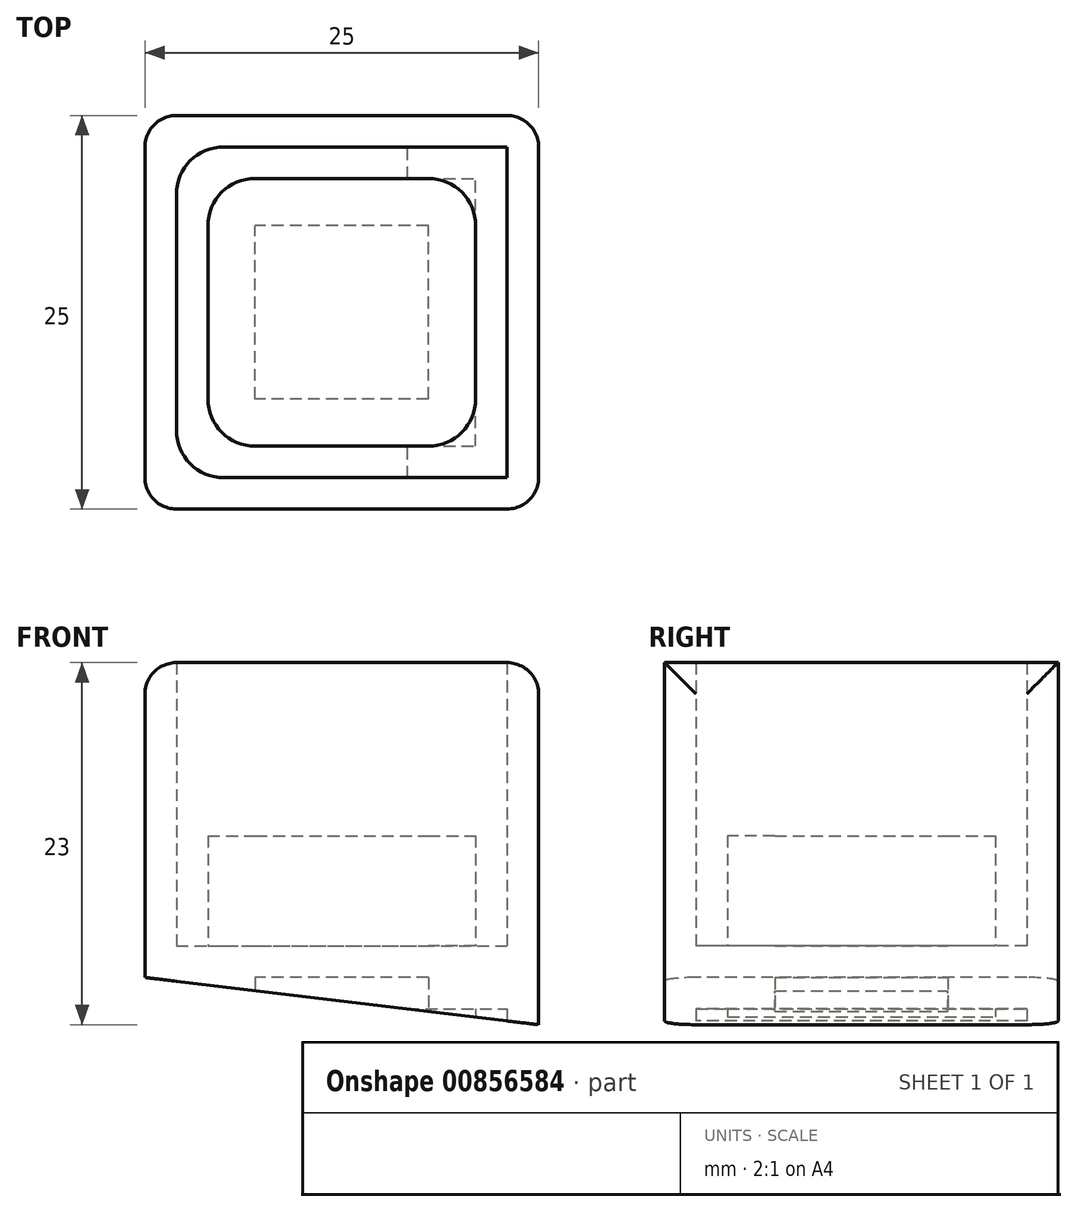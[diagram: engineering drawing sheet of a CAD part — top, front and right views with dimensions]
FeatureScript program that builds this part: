
annotation { "Feature Type Name" : "Feature", "Feature Type Description" : "" }
export const myFeature = defineFeature(function(context is Context, id is Id, definition is map)
    precondition{}
    {
        {
            var Q0;
            Q0=qCreatedBy(makeId("Top.planeOp"),FACE);
            var sketch = newSketch(context, id + "F0", { "sketchPlane" : qUnion([Q0])});
            skLineSegment(sketch, "E0.bottom", {"start": v(0, 0) * mm, "end": v(25, 0) * mm});
            skLineSegment(sketch, "E0.top", {"start": v(0, -25) * mm, "end": v(25, -25) * mm});
            skLineSegment(sketch, "E0.left", {"start": v(0, 0) * mm, "end": v(0, -25) * mm});
            skLineSegment(sketch, "E0.right", {"start": v(25, 0) * mm, "end": v(25, -25) * mm});
            skLineSegment(sketch, "E1.bottom", {"start": v(2, -2) * mm, "end": v(23, -2) * mm});
            skLineSegment(sketch, "E1.top", {"start": v(2, -23) * mm, "end": v(23, -23) * mm});
            skLineSegment(sketch, "E1.left", {"start": v(2, -2) * mm, "end": v(2, -23) * mm});
            skLineSegment(sketch, "E1.right", {"start": v(23, -2) * mm, "end": v(23, -23) * mm});
            skLineSegment(sketch, "E2.bottom", {"start": v(4, -21) * mm, "end": v(21, -21) * mm});
            skLineSegment(sketch, "E2.top", {"start": v(4, -4) * mm, "end": v(21, -4) * mm});
            skLineSegment(sketch, "E2.left", {"start": v(4, -21) * mm, "end": v(4, -4) * mm});
            skLineSegment(sketch, "E2.right", {"start": v(21, -21) * mm, "end": v(21, -4) * mm});
            skLineSegment(sketch, "E3.bottom", {"start": v(18, -18) * mm, "end": v(7, -18) * mm});
            skLineSegment(sketch, "E3.top", {"start": v(18, -7) * mm, "end": v(7, -7) * mm});
            skLineSegment(sketch, "E3.left", {"start": v(18, -18) * mm, "end": v(18, -7) * mm});
            skLineSegment(sketch, "E3.right", {"start": v(7, -18) * mm, "end": v(7, -7) * mm});
            skSolve(sketch);
        }
        {
            var Q0;
            Q0 = qSketchRegion(id + "F0", true);
            extrude(context, id + "F1", {"entities" : qUnion([Q0]), "depth" : 23 * mm, "offsetDistance" : 25 * mm});
        }
        {
            var Q0;
            Q0=makeQuery(id+"F0.imprint","IMPRINT",FACE,{"disambiguationData":[TD([[makeQuery(id+"F0.imprint","IMPRINT",EDGE,{"derivedFrom":sQuery(id+"F0.wireOp",EDGE,"E1.bottom")}),-1.0]])]});
            extrude(context, id + "F2", {"entities" : qUnion([Q0]), "operationType" : NewBodyOperationType.ADD, "depth" : 5 * mm, "offsetDistance" : 25 * mm});
        }
        {
            var Q0;
            Q0=makeQuery(id+"F0.imprint","IMPRINT",FACE,{"disambiguationData":[TD([[makeQuery(id+"F0.imprint","IMPRINT",EDGE,{"derivedFrom":sQuery(id+"F0.wireOp",EDGE,"E2.bottom")}),1.0]])]});
            var Q1;
            Q1=makeQuery(id+"F0.imprint","IMPRINT",FACE,{"disambiguationData":[TD([[makeQuery(id+"F0.imprint","IMPRINT",EDGE,{"derivedFrom":sQuery(id+"F0.wireOp",EDGE,"E3.bottom")}),-1.0]])]});
            extrude(context, id + "F3", {"entities" : qUnion([Q0, Q1]), "operationType" : NewBodyOperationType.ADD, "depth" : 12 * mm, "offsetDistance" : 25 * mm});
        }
        {
            var Q0;
            Q0=makeQuery(id+"F0.imprint","IMPRINT",FACE,{"disambiguationData":[TD([[makeQuery(id+"F0.imprint","IMPRINT",EDGE,{"derivedFrom":sQuery(id+"F0.wireOp",EDGE,"E3.bottom")}),-1.0]])]});
            extrude(context, id + "F4", {"entities" : qUnion([Q0]), "operationType" : NewBodyOperationType.REMOVE, "depth" : 3 * mm, "offsetDistance" : 25 * mm});
        }
        {
            var Q0;
            Q0=makeQuery(id+"F0.imprint","IMPRINT",FACE,{"disambiguationData":[TD([[makeQuery(id+"F0.imprint","IMPRINT",EDGE,{"derivedFrom":sQuery(id+"F0.wireOp",EDGE,"E1.bottom")}),-1.0]])]});
            extrude(context, id + "F5", {"entities" : qUnion([Q0]), "operationType" : NewBodyOperationType.REMOVE, "depth" : 1 * mm, "offsetDistance" : 25 * mm});
        }
        {
            var Q0;
            Q0=makeQuery(id+"F1.opExtrude","SWEPT_FACE",FACE,{"disambiguationData":[OSD([sQuery(id+"F0.wireOp",EDGE,"E0.top")])]});
            var sketch = newSketch(context, id + "F6", { "sketchPlane" : qUnion([Q0])});
            skLineSegment(sketch, "E4.bottom", {"start": v(0, 23) * mm, "end": v(25, 23) * mm});
            skLineSegment(sketch, "E4.top", {"start": v(0, 0) * mm, "end": v(25, 0) * mm});
            skLineSegment(sketch, "E4.left", {"start": v(0, 23) * mm, "end": v(0, 0) * mm});
            skLineSegment(sketch, "E4.right", {"start": v(25, 23) * mm, "end": v(25, 0) * mm});
            skLineSegment(sketch, "E5", {"start": v(25, 0) * mm, "end": v(0, 3) * mm});
            skSolve(sketch);
        }
        {
            var Q0;
            {var subQ0=sQuery(id+"F6.wireOp",EDGE,"E4.top");Q0=makeQuery(id+"F6.imprint","IMPRINT",FACE,{"disambiguationData":[TD([[makeQuery(id+"F6.imprint","IMPRINT",EDGE,{"derivedFrom":subQ0}),1.0]])]});}
            var Q1;
            Q1=makeQuery(id+"F1.opExtrude","SWEPT_FACE",FACE,{"disambiguationData":[OSD([sQuery(id+"F0.wireOp",EDGE,"E0.bottom")])]});
            extrude(context, id + "F7", {"entities" : qUnion([Q0]), "operationType" : NewBodyOperationType.REMOVE, "endBound" : BoundingType.UP_TO_SURFACE, "oppositeDirection" : true, "depth" : 25 * mm, "endBoundEntityFace" : qUnion([Q1]), "offsetDistance" : 25 * mm});
        }
        {
            var Q0;
            Q0=makeQuery(id+"F1.opExtrude","SWEPT_EDGE",EDGE,{"disambiguationData":[OSD([sQuery(id+"F0.wireOp",EDGE,"E0.top"),sQuery(id+"F0.wireOp",EDGE,"E0.right")])]});
            var Q1;
            Q1=makeQuery(id+"F1.opExtrude","SWEPT_EDGE",EDGE,{"disambiguationData":[OSD([sQuery(id+"F0.wireOp",EDGE,"E0.top"),sQuery(id+"F0.wireOp",EDGE,"E0.left")])]});
            var Q2;
            Q2=makeQuery(id+"F1.opExtrude","SWEPT_EDGE",EDGE,{"disambiguationData":[OSD([sQuery(id+"F0.wireOp",EDGE,"E0.bottom"),sQuery(id+"F0.wireOp",EDGE,"E0.left")])]});
            var Q3;
            Q3=makeQuery(id+"F1.opExtrude","SWEPT_EDGE",EDGE,{"disambiguationData":[OSD([sQuery(id+"F0.wireOp",EDGE,"E0.bottom"),sQuery(id+"F0.wireOp",EDGE,"E0.right")])]});
            var Q4;
            Q4=makeQuery(id+"F1.opExtrude","CAP_EDGE",EDGE,{"disambiguationData":[OSD([sQuery(id+"F0.wireOp",EDGE,"E0.left")])],"isStart":false});
            var Q5;
            Q5=makeQuery(id+"F1.opExtrude","CAP_EDGE",EDGE,{"disambiguationData":[OSD([sQuery(id+"F0.wireOp",EDGE,"E0.right")])],"isStart":false});
            fillet(context, id + "F8", {"entities" : qUnion([Q0, Q1, Q2, Q3, Q4, Q5]), "radius" : 2 * mm, "tangentPropagation" : true, "allowEdgeOverflow" : false});
        }
        {
            var Q0;
            Q0=makeQuery(id+"F1.opExtrude","SWEPT_EDGE",EDGE,{"disambiguationData":[OSD([sQuery(id+"F0.wireOp",EDGE,"E1.bottom"),sQuery(id+"F0.wireOp",EDGE,"E1.left")])]});
            var Q1;
            Q1=makeQuery(id+"F3.opExtrude","SWEPT_EDGE",EDGE,{"disambiguationData":[OSD([sQuery(id+"F0.wireOp",EDGE,"E2.top"),sQuery(id+"F0.wireOp",EDGE,"E2.left")])]});
            var Q2;
            Q2=makeQuery(id+"F3.opExtrude","SWEPT_EDGE",EDGE,{"disambiguationData":[OSD([sQuery(id+"F0.wireOp",EDGE,"E2.top"),sQuery(id+"F0.wireOp",EDGE,"E2.right")])]});
            var Q3;
            Q3=makeQuery(id+"F3.opExtrude","SWEPT_EDGE",EDGE,{"disambiguationData":[OSD([sQuery(id+"F0.wireOp",EDGE,"E2.bottom"),sQuery(id+"F0.wireOp",EDGE,"E2.right")])]});
            var Q4;
            Q4=makeQuery(id+"F3.opExtrude","SWEPT_EDGE",EDGE,{"disambiguationData":[OSD([sQuery(id+"F0.wireOp",EDGE,"E2.bottom"),sQuery(id+"F0.wireOp",EDGE,"E2.left")])]});
            var Q5;
            Q5=makeQuery(id+"F1.opExtrude","SWEPT_EDGE",EDGE,{"disambiguationData":[OSD([sQuery(id+"F0.wireOp",EDGE,"E1.top"),sQuery(id+"F0.wireOp",EDGE,"E1.left")])]});
            fillet(context, id + "F9", {"entities" : qUnion([Q0, Q1, Q2, Q3, Q4, Q5]), "radius" : 3 * mm, "tangentPropagation" : true, "allowEdgeOverflow" : false});
        }
    });
